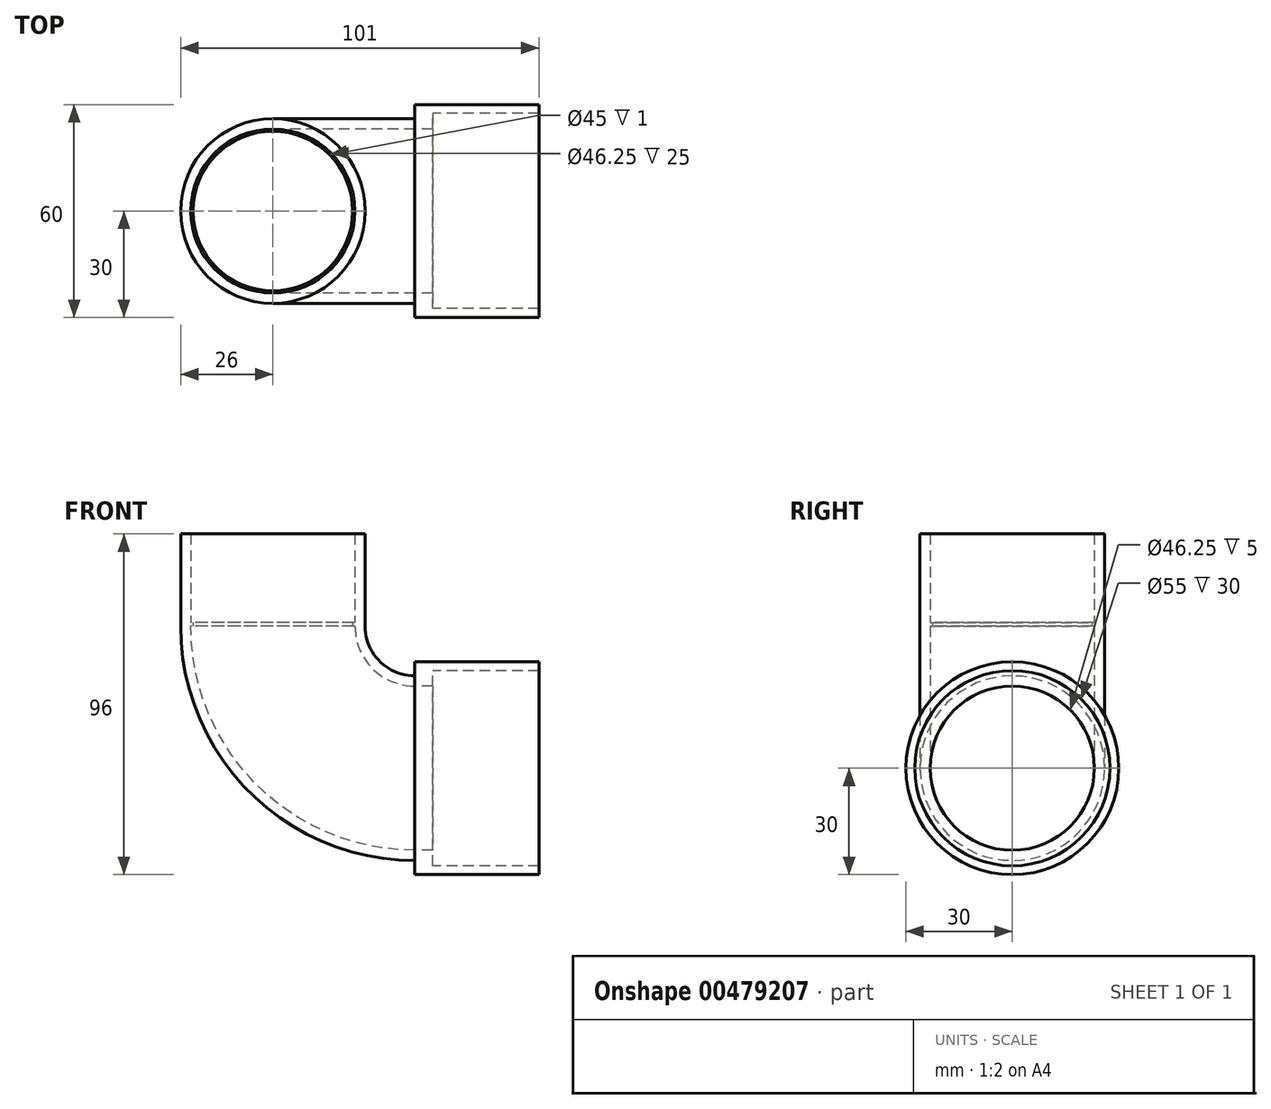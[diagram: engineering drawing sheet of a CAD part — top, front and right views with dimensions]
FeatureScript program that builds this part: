
annotation { "Feature Type Name" : "Feature", "Feature Type Description" : "" }
export const myFeature = defineFeature(function(context is Context, id is Id, definition is map)
    precondition{}
    {
        {
            var Q0;
            Q0=qCreatedBy(makeId("Top.planeOp"),FACE);
            var sketch = newSketch(context, id + "F0", { "sketchPlane" : qUnion([Q0])});
            skCircle(sketch, "E0", {"center": v(0, 0) * mm, "radius": 23.12 * mm});
            skCircle(sketch, "E1", {"center": v(0, 0) * mm, "radius": 26 * mm});
            skSolve(sketch);
        }
        {
            var Q0;
            Q0=qCreatedBy(makeId("Front.planeOp"),FACE);
            var sketch = newSketch(context, id + "F1", { "sketchPlane" : qUnion([Q0])});
            skArc(sketch, "E2", {"start": v(0, 0) * mm, "mid": v(11.72, -28.28) * mm, "end": v(40, -40) * mm});
            skSolve(sketch);
        }
        {
            var Q0;
            Q0=makeQuery(id+"F0.imprint","IMPRINT",FACE,{"disambiguationData":[TD([[makeQuery(id+"F0.imprint","IMPRINT",EDGE,{"derivedFrom":sQuery(id+"F0.wireOp",EDGE,"E0")}),-1.0]])]});
            var Q1;
            Q1=sQuery(id+"F1.wireOp",EDGE,"E2");
            sweep(context, id + "F2", {"profiles" : qUnion([Q0]), "path" : qUnion([Q1])});
        }
        {
            var Q0;
            Q0=makeQuery(id+"F2.opSweep","CAP_FACE",FACE,{"disambiguationData":[OSD([sQuery(id+"F0.wireOp",EDGE,"E0"),sQuery(id+"F0.wireOp",EDGE,"E1"),sQuery(id+"F1.wireOp",VERTEX,"E2.start")])],"isStart":true});
            var sketch = newSketch(context, id + "F3", { "sketchPlane" : qUnion([Q0])});
            skCircle(sketch, "E3", {"center": v(0, 0) * mm, "radius": 22.5 * mm});
            skSolve(sketch);
        }
        {
            var Q0;
            Q0=makeQuery(id+"F3.imprint","IMPRINT",FACE,{"disambiguationData":[TD([[makeQuery(id+"F3.imprint","IMPRINT",EDGE,{"derivedFrom":sQuery(id+"F3.wireOp",EDGE,"E3")}),-1.0]])]});
            var Q1;
            {var subQ0=sQuery(id+"F1.wireOp",VERTEX,"E2.start");Q1=makeQuery(id+"F3.imprint","IMPRINT",FACE,{"disambiguationData":[TD([[makeQuery(id+"F3.imprint","IMPRINT",EDGE,{"derivedFrom":makeQuery(id+"F2.opSweep","CAP_EDGE",EDGE,{"disambiguationData":[OSD([sQuery(id+"F0.wireOp",EDGE,"E0"),subQ0])],"isStart":true})}),-1.0]])]});}
            extrude(context, id + "F4", {"entities" : qUnion([Q0, Q1]), "operationType" : NewBodyOperationType.ADD, "depth" : 1 * mm, "offsetDistance" : 25 * mm});
        }
        {
            var Q0;
            Q0=makeQuery(id+"F4.opExtrude","CAP_FACE",FACE,{"disambiguationData":[OSD([sQuery(id+"F0.wireOp",EDGE,"E1"),sQuery(id+"F1.wireOp",VERTEX,"E2.start"),sQuery(id+"F3.wireOp",EDGE,"E3")])],"isStart":false});
            var sketch = newSketch(context, id + "F5", { "sketchPlane" : qUnion([Q0])});
            skCircle(sketch, "E4", {"center": v(0, 0) * mm, "radius": 23.12 * mm});
            skCircle(sketch, "E5", {"center": v(0, 0) * mm, "radius": 26 * mm});
            skSolve(sketch);
        }
        {
            var Q0;
            Q0=makeQuery(id+"F5.imprint","IMPRINT",FACE,{"disambiguationData":[TD([[makeQuery(id+"F5.imprint","IMPRINT",EDGE,{"derivedFrom":sQuery(id+"F5.wireOp",EDGE,"E4")}),-1.0]])]});
            extrude(context, id + "F6", {"entities" : qUnion([Q0]), "operationType" : NewBodyOperationType.ADD, "depth" : 25 * mm, "offsetDistance" : 25 * mm});
        }
        {
            var Q0;
            Q0=makeQuery(id+"F2.opSweep","CAP_FACE",FACE,{"disambiguationData":[OSD([sQuery(id+"F0.wireOp",EDGE,"E0"),sQuery(id+"F0.wireOp",EDGE,"E1"),sQuery(id+"F1.wireOp",VERTEX,"E2.end")])],"isStart":false});
            var sketch = newSketch(context, id + "F7", { "sketchPlane" : qUnion([Q0])});
            skCircle(sketch, "E6", {"center": v(0, -40) * mm, "radius": 27.5 * mm});
            skCircle(sketch, "E7", {"center": v(0, -40) * mm, "radius": 30 * mm});
            skSolve(sketch);
        }
        {
            var Q0;
            {var subQ0=sQuery(id+"F1.wireOp",VERTEX,"E2.end");Q0=makeQuery(id+"F7.imprint","IMPRINT",FACE,{"disambiguationData":[TD([[makeQuery(id+"F7.imprint","IMPRINT",EDGE,{"derivedFrom":makeQuery(id+"F2.opSweep","CAP_EDGE",EDGE,{"disambiguationData":[OSD([sQuery(id+"F0.wireOp",EDGE,"E0"),subQ0])],"isStart":false})}),1.0]])]});}
            var Q1;
            Q1=makeQuery(id+"F7.imprint","IMPRINT",FACE,{"disambiguationData":[TD([[makeQuery(id+"F7.imprint","IMPRINT",EDGE,{"derivedFrom":sQuery(id+"F7.wireOp",EDGE,"E6")}),1.0]])]});
            extrude(context, id + "F8", {"entities" : qUnion([Q0, Q1]), "operationType" : NewBodyOperationType.ADD, "depth" : 5 * mm, "offsetDistance" : 25 * mm});
        }
        {
            var Q0;
            Q0=makeQuery(id+"F7.imprint","IMPRINT",FACE,{"disambiguationData":[TD([[makeQuery(id+"F7.imprint","IMPRINT",EDGE,{"derivedFrom":sQuery(id+"F7.wireOp",EDGE,"E6")}),-1.0]])]});
            extrude(context, id + "F9", {"entities" : qUnion([Q0]), "operationType" : NewBodyOperationType.ADD, "depth" : 35 * mm, "offsetDistance" : 25 * mm});
        }
    });
